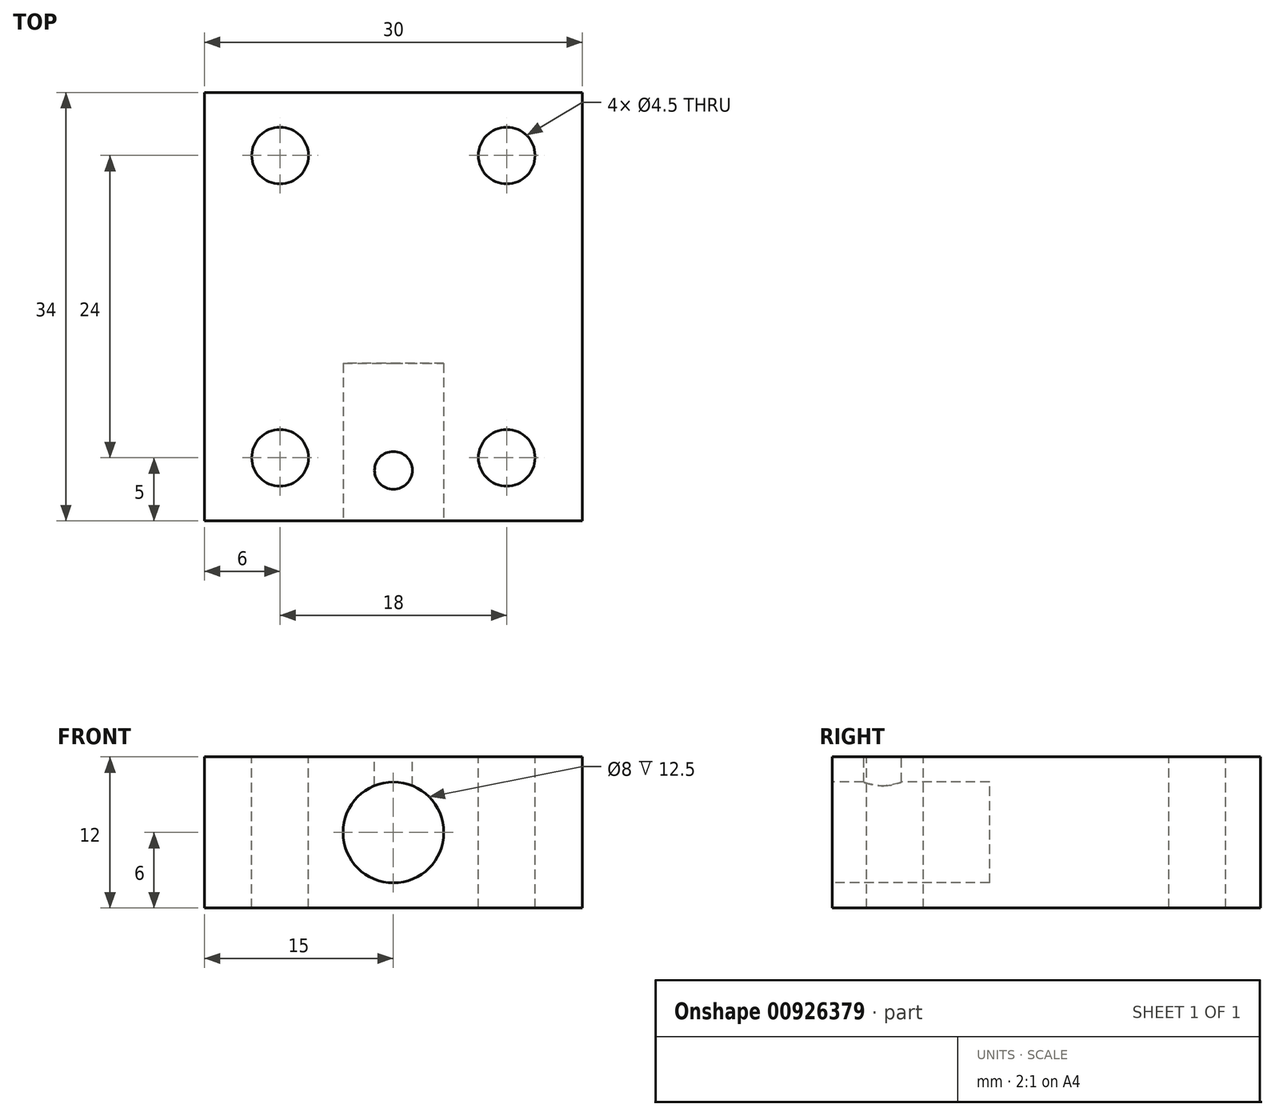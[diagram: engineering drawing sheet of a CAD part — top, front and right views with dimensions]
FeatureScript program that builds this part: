
annotation { "Feature Type Name" : "Feature", "Feature Type Description" : "" }
export const myFeature = defineFeature(function(context is Context, id is Id, definition is map)
    precondition{}
    {
        {
            var Q0;
            Q0=qCreatedBy(makeId("Top.planeOp"),FACE);
            var sketch = newSketch(context, id + "F0", { "sketchPlane" : qUnion([Q0])});
            skLineSegment(sketch, "E0.bottom", {"start": v(0, 0) * mm, "end": v(30, 0) * mm});
            skLineSegment(sketch, "E0.top", {"start": v(0, 34) * mm, "end": v(30, 34) * mm});
            skLineSegment(sketch, "E0.left", {"start": v(0, 0) * mm, "end": v(0, 34) * mm});
            skLineSegment(sketch, "E0.right", {"start": v(30, 0) * mm, "end": v(30, 34) * mm});
            skSolve(sketch);
        }
        {
            var Q0;
            Q0 = qSketchRegion(id + "F0", true);
            extrude(context, id + "F1", {"entities" : qUnion([Q0]), "depth" : 12 * mm, "offsetDistance" : 25 * mm});
        }
        {
            var Q0;
            Q0=makeQuery(id+"F1.opExtrude","CAP_FACE",FACE,{"disambiguationData":[OSD([sQuery(id+"F0.wireOp",EDGE,"E0.bottom"),sQuery(id+"F0.wireOp",EDGE,"E0.top"),sQuery(id+"F0.wireOp",EDGE,"E0.left"),sQuery(id+"F0.wireOp",EDGE,"E0.right")])],"isStart":false});
            var sketch = newSketch(context, id + "F2", { "sketchPlane" : qUnion([Q0])});
            skLineSegment(sketch, "E1", {"start": v(6, 34) * mm, "end": v(6, 0) * mm, "construction": true});
            skLineSegment(sketch, "E2", {"start": v(24, 34) * mm, "end": v(24, 0) * mm, "construction": true});
            skLineSegment(sketch, "E3", {"start": v(0, 29) * mm, "end": v(30, 29) * mm, "construction": true});
            skLineSegment(sketch, "E4", {"start": v(0, 5) * mm, "end": v(30, 5) * mm, "construction": true});
            skCircle(sketch, "E5", {"center": v(6, 29) * mm, "radius": 2.25 * mm});
            skCircle(sketch, "E6", {"center": v(24, 29) * mm, "radius": 2.25 * mm});
            skCircle(sketch, "E7", {"center": v(24, 5) * mm, "radius": 2.25 * mm});
            skCircle(sketch, "E8", {"center": v(6, 5) * mm, "radius": 2.25 * mm});
            skSolve(sketch);
        }
        {
            var Q0;
            Q0 = qSketchRegion(id + "F2", true);
            extrude(context, id + "F3", {"entities" : qUnion([Q0]), "operationType" : NewBodyOperationType.REMOVE, "endBound" : BoundingType.THROUGH_ALL, "oppositeDirection" : true, "depth" : 25 * mm, "offsetDistance" : 25 * mm});
        }
        {
            var Q0;
            Q0=makeQuery(id+"F1.opExtrude","SWEPT_FACE",FACE,{"disambiguationData":[OSD([sQuery(id+"F0.wireOp",EDGE,"E0.bottom")])]});
            var sketch = newSketch(context, id + "F4", { "sketchPlane" : qUnion([Q0])});
            skLineSegment(sketch, "E9", {"start": v(15, 12) * mm, "end": v(15, 0) * mm, "construction": true});
            skLineSegment(sketch, "E10", {"start": v(0, 6) * mm, "end": v(30, 6) * mm, "construction": true});
            skCircle(sketch, "E11", {"center": v(15, 6) * mm, "radius": 4 * mm});
            skSolve(sketch);
        }
        {
            var Q0;
            Q0 = qSketchRegion(id + "F4", true);
            extrude(context, id + "F5", {"entities" : qUnion([Q0]), "operationType" : NewBodyOperationType.REMOVE, "oppositeDirection" : true, "depth" : 12.5 * mm, "offsetDistance" : 25 * mm});
        }
        {
            var Q0;
            Q0=makeQuery(id+"F1.opExtrude","CAP_FACE",FACE,{"disambiguationData":[OSD([sQuery(id+"F0.wireOp",EDGE,"E0.bottom"),sQuery(id+"F0.wireOp",EDGE,"E0.top"),sQuery(id+"F0.wireOp",EDGE,"E0.left"),sQuery(id+"F0.wireOp",EDGE,"E0.right")])],"isStart":false});
            var sketch = newSketch(context, id + "F6", { "sketchPlane" : qUnion([Q0])});
            skLineSegment(sketch, "E12", {"start": v(15, 0) * mm, "end": v(15, 34) * mm, "construction": true});
            skLineSegment(sketch, "E13", {"start": v(0, 4) * mm, "end": v(30, 4) * mm, "construction": true});
            skCircle(sketch, "E14", {"center": v(15, 4) * mm, "radius": 1.5 * mm});
            skSolve(sketch);
        }
        {
            var Q0;
            Q0=makeQuery(id+"F6.imprint","IMPRINT",FACE,{"disambiguationData":[TD([[makeQuery(id+"F6.imprint","IMPRINT",EDGE,{"derivedFrom":sQuery(id+"F6.wireOp",EDGE,"E14")}),1.0]])]});
            extrude(context, id + "F7", {"entities" : qUnion([Q0]), "operationType" : NewBodyOperationType.REMOVE, "oppositeDirection" : true, "depth" : 6 * mm, "offsetDistance" : 25 * mm});
        }
    });
